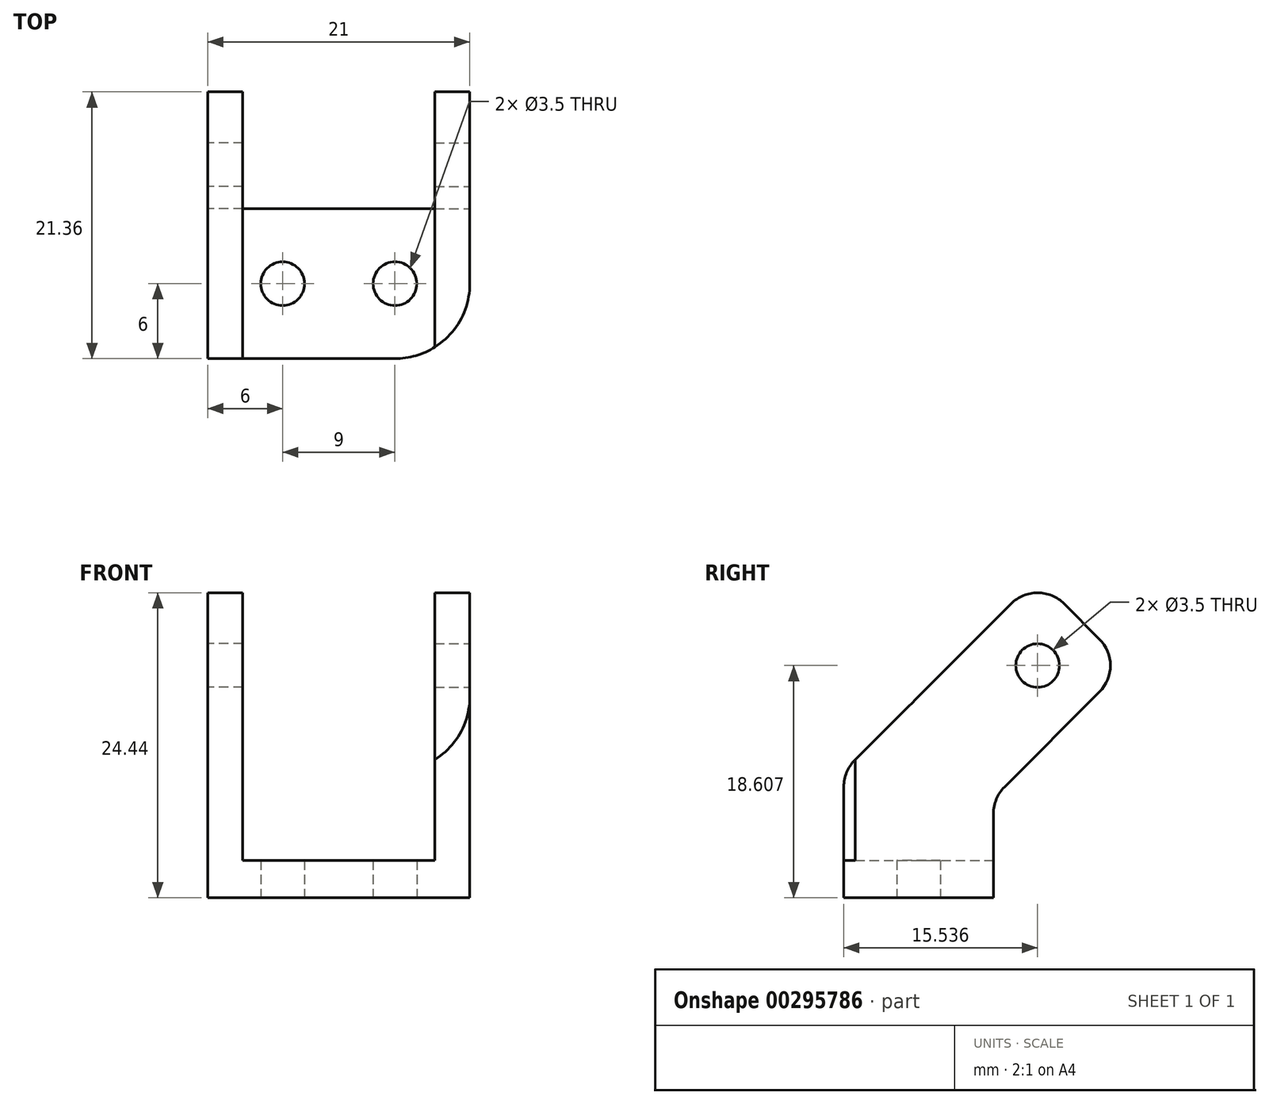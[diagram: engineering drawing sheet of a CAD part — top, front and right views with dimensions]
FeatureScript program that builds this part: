
annotation { "Feature Type Name" : "Feature", "Feature Type Description" : "" }
export const myFeature = defineFeature(function(context is Context, id is Id, definition is map)
    precondition{}
    {
        {
            var Q0;
            Q0=qCreatedBy(makeId("Top.planeOp"),FACE);
            var sketch = newSketch(context, id + "F0", { "sketchPlane" : qUnion([Q0])});
            skLineSegment(sketch, "E0.bottom", {"start": v(0, 0) * mm, "end": v(21, 0) * mm});
            skLineSegment(sketch, "E0.top", {"start": v(0, 12) * mm, "end": v(21, 12) * mm});
            skLineSegment(sketch, "E0.left", {"start": v(0, 0) * mm, "end": v(0, 12) * mm});
            skLineSegment(sketch, "E0.right", {"start": v(21, 0) * mm, "end": v(21, 12) * mm});
            skCircle(sketch, "E1", {"center": v(6, 6) * mm, "radius": 1.75 * mm});
            skPoint(sketch, "E1.centerSnap0", {"position": v(0, 6) * mm});
            skCircle(sketch, "E2", {"center": v(15, 6) * mm, "radius": 1.75 * mm});
            skSolve(sketch);
        }
        {
            var Q0;
            Q0 = qSketchRegion(id + "F0", true);
            extrude(context, id + "F1", {"entities" : qUnion([Q0]), "depth" : 3 * mm});
        }
        {
            var Q0;
            Q0=makeQuery(id+"F1.opExtrude","SWEPT_FACE",FACE,{"disambiguationData":[OSD([sQuery(id+"F0.wireOp",EDGE,"E0.left")])]});
            var sketch = newSketch(context, id + "F2", { "sketchPlane" : qUnion([Q0])});
            skLineSegment(sketch, "E3", {"start": v(-12, 3) * mm, "end": v(-12, 8) * mm});
            skLineSegment(sketch, "E4", {"start": v(-12, 8) * mm, "end": v(-22.6, 18.6) * mm});
            skLineSegment(sketch, "E5", {"start": v(-12, 3) * mm, "end": v(0, 3) * mm});
            skLineSegment(sketch, "E6", {"start": v(-22.6, 18.6) * mm, "end": v(-15.54, 25.68) * mm});
            skLineSegment(sketch, "E7", {"start": v(-15.54, 25.68) * mm, "end": v(0, 10.14) * mm});
            skLineSegment(sketch, "E8", {"start": v(0, 10.14) * mm, "end": v(0, 3) * mm});
            skCircle(sketch, "E9", {"center": v(-15.54, 18.6) * mm, "radius": 1.75 * mm});
            skLineSegment(sketch, "E10.0", {"start": v(-7.75, 3) * mm, "end": v(-4.25, 3) * mm, "construction": true});
            skLineSegment(sketch, "E11", {"start": v(-7.75, 0) * mm, "end": v(-7.75, 3) * mm, "construction": true});
            skLineSegment(sketch, "E12", {"start": v(-4.25, 3) * mm, "end": v(-4.25, 0) * mm, "construction": true});
            skSolve(sketch);
        }
        {
            var Q0;
            Q0=makeQuery(id+"F1.opExtrude","SWEPT_FACE",FACE,{"disambiguationData":[OSD([sQuery(id+"F0.wireOp",EDGE,"E0.right")])]});
            var sketch = newSketch(context, id + "F3", { "sketchPlane" : qUnion([Q0])});
            skLineSegment(sketch, "E13.0.0", {"start": v(0, 3) * mm, "end": v(0, 10.14) * mm});
            skLineSegment(sketch, "E13.0.1", {"start": v(0, 10.14) * mm, "end": v(15.54, 25.68) * mm});
            skLineSegment(sketch, "E13.0.2", {"start": v(15.54, 25.68) * mm, "end": v(22.6, 18.6) * mm});
            skLineSegment(sketch, "E13.0.3", {"start": v(22.6, 18.6) * mm, "end": v(12, 8) * mm});
            skLineSegment(sketch, "E13.0.4", {"start": v(12, 8) * mm, "end": v(12, 3) * mm});
            skLineSegment(sketch, "E13.0.5", {"start": v(12, 3) * mm, "end": v(0, 3) * mm});
            skCircle(sketch, "E14.0", {"center": v(15.54, 18.6) * mm, "radius": 1.75 * mm});
            skSolve(sketch);
        }
        {
            var Q0;
            Q0 = qSketchRegion(id + "F3", true);
            extrude(context, id + "F4", {"entities" : qUnion([Q0]), "operationType" : NewBodyOperationType.ADD, "oppositeDirection" : true, "depth" : 2.8 * mm});
        }
        {
            var Q0;
            Q0=makeQuery(id+"F2.imprint","IMPRINT",FACE,{"disambiguationData":[TD([[makeQuery(id+"F2.imprint","IMPRINT",EDGE,{"derivedFrom":sQuery(id+"F2.wireOp",EDGE,"E3")}),-1.0]])]});
            extrude(context, id + "F5", {"entities" : qUnion([Q0]), "operationType" : NewBodyOperationType.ADD, "oppositeDirection" : true, "depth" : 2.8 * mm});
        }
        {
            var Q0;
            Q0=makeQuery(id+"F4.boolean.opBoolean","MERGE",EDGE,{"derivedFrom":[makeQuery(id+"F1.opExtrude","SWEPT_EDGE",EDGE,{"disambiguationData":[OSD([sQuery(id+"F0.wireOp",EDGE,"E0.bottom"),sQuery(id+"F0.wireOp",EDGE,"E0.right")])]}),makeQuery(id+"F4.opExtrude","CAP_EDGE",EDGE,{"disambiguationData":[OSD([sQuery(id+"F3.wireOp",EDGE,"E13.0.0")])],"isStart":true})]});
            fillet(context, id + "F6", {"entities" : qUnion([Q0]), "radius" : 6 * mm, "tangentPropagation" : true, "allowEdgeOverflow" : false});
        }
        {
            var Q0;
            Q0=makeQuery(id+"F4.opExtrude","SWEPT_EDGE",EDGE,{"disambiguationData":[OSD([sQuery(id+"F3.wireOp",EDGE,"E13.0.3"),sQuery(id+"F3.wireOp",EDGE,"E13.0.4")])]});
            var Q1;
            Q1=makeQuery(id+"F5.opExtrude","SWEPT_EDGE",EDGE,{"disambiguationData":[OSD([sQuery(id+"F2.wireOp",EDGE,"E3"),sQuery(id+"F2.wireOp",EDGE,"E4")])]});
            var Q2;
            Q2=makeQuery(id+"F5.opExtrude","SWEPT_EDGE",EDGE,{"disambiguationData":[OSD([sQuery(id+"F2.wireOp",EDGE,"E4"),sQuery(id+"F2.wireOp",EDGE,"E6")])]});
            var Q3;
            Q3=makeQuery(id+"F5.opExtrude","SWEPT_EDGE",EDGE,{"disambiguationData":[OSD([sQuery(id+"F2.wireOp",EDGE,"E6"),sQuery(id+"F2.wireOp",EDGE,"E7")])]});
            var Q4;
            Q4=makeQuery(id+"F4.opExtrude","SWEPT_EDGE",EDGE,{"disambiguationData":[OSD([sQuery(id+"F3.wireOp",EDGE,"E13.0.2"),sQuery(id+"F3.wireOp",EDGE,"E13.0.3")])]});
            var Q5;
            Q5=makeQuery(id+"F4.opExtrude","SWEPT_EDGE",EDGE,{"disambiguationData":[OSD([sQuery(id+"F3.wireOp",EDGE,"E13.0.1"),sQuery(id+"F3.wireOp",EDGE,"E13.0.2")])]});
            var Q6;
            Q6=makeQuery(id+"F4.opExtrude","SWEPT_EDGE",EDGE,{"disambiguationData":[OSD([sQuery(id+"F3.wireOp",EDGE,"E13.0.0"),sQuery(id+"F3.wireOp",EDGE,"E13.0.1")])]});
            var Q7;
            Q7=makeQuery(id+"F5.opExtrude","SWEPT_EDGE",EDGE,{"disambiguationData":[OSD([sQuery(id+"F2.wireOp",EDGE,"E7"),sQuery(id+"F2.wireOp",EDGE,"E8")])]});
            fillet(context, id + "F7", {"entities" : qUnion([Q0, Q1, Q2, Q3, Q4, Q5, Q6, Q7]), "radius" : 3 * mm, "tangentPropagation" : true, "allowEdgeOverflow" : false});
        }
    });
